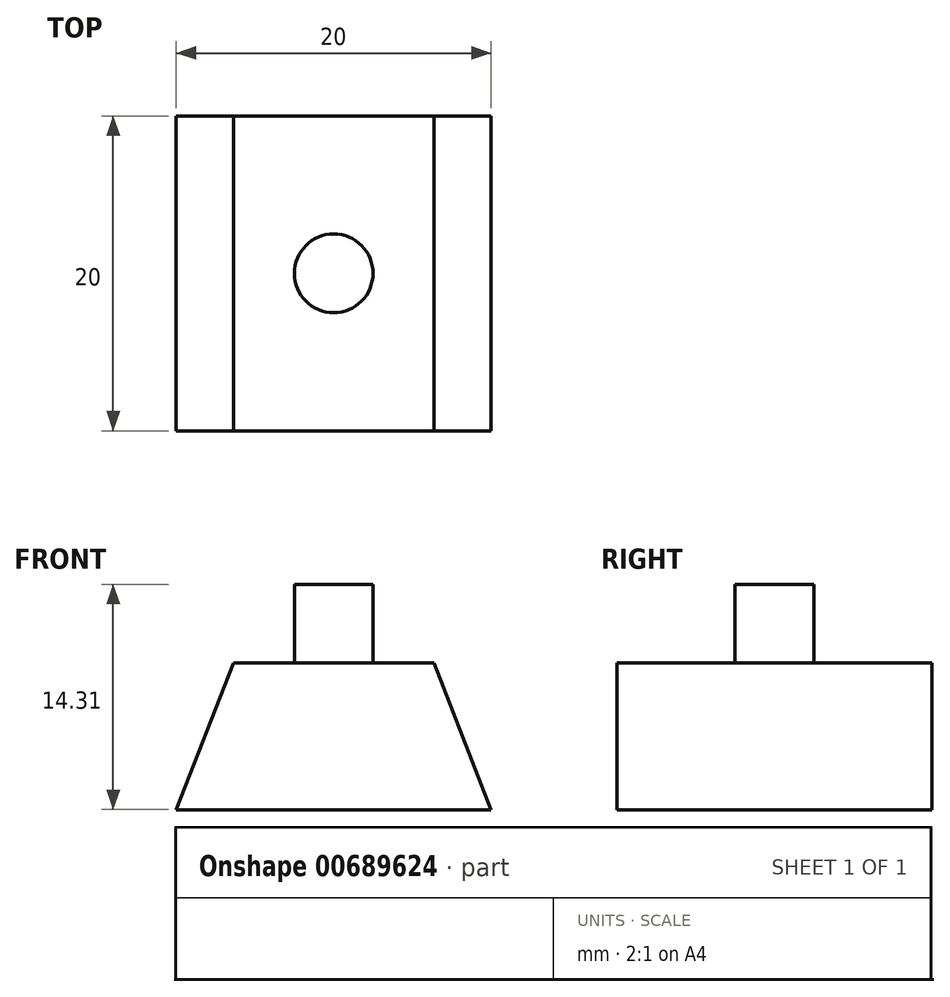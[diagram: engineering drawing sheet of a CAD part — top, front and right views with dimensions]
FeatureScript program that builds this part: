
annotation { "Feature Type Name" : "Feature", "Feature Type Description" : "" }
export const myFeature = defineFeature(function(context is Context, id is Id, definition is map)
    precondition{}
    {
        {
            var Q0;
            Q0=qCreatedBy(makeId("Front.planeOp"),FACE);
            var sketch = newSketch(context, id + "F0", { "sketchPlane" : qUnion([Q0])});
            skLineSegment(sketch, "E0", {"start": v(0, 0) * mm, "end": v(6.36, 0) * mm});
            skLineSegment(sketch, "E1", {"start": v(0, 0) * mm, "end": v(-6.36, 0) * mm});
            skLineSegment(sketch, "E2", {"start": v(0, -9.31) * mm, "end": v(10, -9.31) * mm});
            skLineSegment(sketch, "E3", {"start": v(0, -9.31) * mm, "end": v(-10, -9.31) * mm});
            skLineSegment(sketch, "E4", {"start": v(-6.36, 0) * mm, "end": v(-10, -9.31) * mm});
            skLineSegment(sketch, "E5", {"start": v(6.36, 0) * mm, "end": v(10, -9.31) * mm});
            skSolve(sketch);
        }
        {
            var Q0;
            Q0=makeQuery(id+"F0.imprint","IMPRINT",FACE,{"disambiguationData":[TD([[makeQuery(id+"F0.imprint","IMPRINT",EDGE,{"derivedFrom":sQuery(id+"F0.wireOp",EDGE,"E0")}),-1.0]])]});
            extrude(context, id + "F1", {"entities" : qUnion([Q0]), "depth" : 20 * mm, "offsetDistance" : 25 * mm});
        }
        {
            var Q0;
            Q0=qCreatedBy(makeId("Top.planeOp"),FACE);
            var sketch = newSketch(context, id + "F2", { "sketchPlane" : qUnion([Q0])});
            skCircle(sketch, "E6", {"center": v(0, -10) * mm, "radius": 2.5 * mm});
            skSolve(sketch);
        }
        {
            var Q0;
            Q0=makeQuery(id+"F2.imprint","IMPRINT",FACE,{"disambiguationData":[TD([[makeQuery(id+"F2.imprint","IMPRINT",EDGE,{"derivedFrom":sQuery(id+"F2.wireOp",EDGE,"E6")}),1.0]])]});
            extrude(context, id + "F3", {"entities" : qUnion([Q0]), "operationType" : NewBodyOperationType.ADD, "depth" : 5 * mm, "offsetDistance" : 25 * mm});
        }
    });
